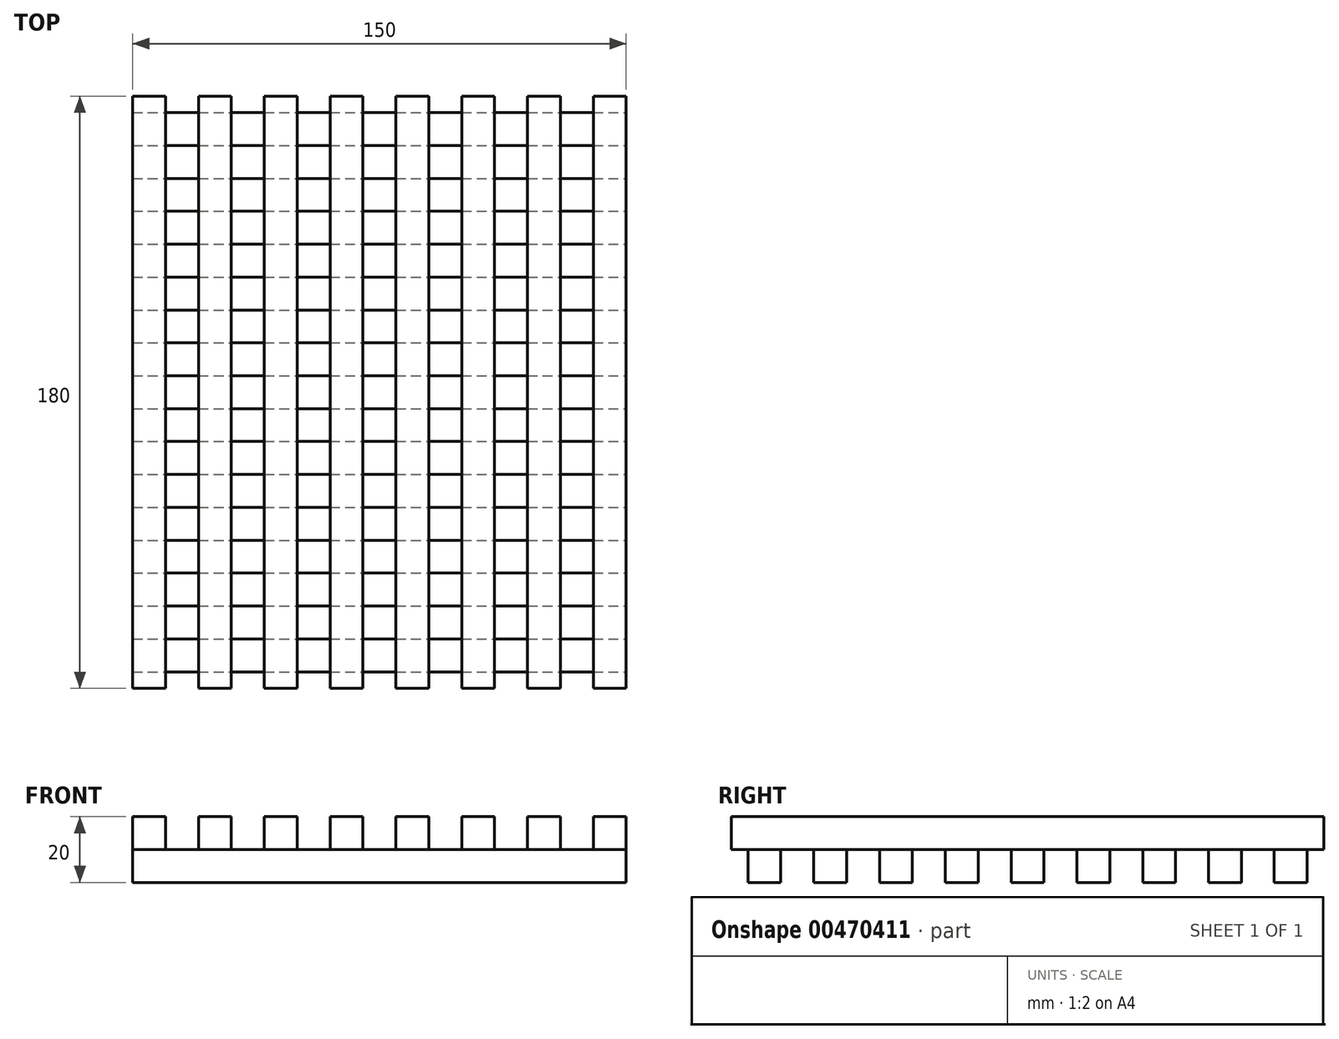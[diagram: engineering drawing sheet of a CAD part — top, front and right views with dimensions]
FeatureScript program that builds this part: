
annotation { "Feature Type Name" : "Feature", "Feature Type Description" : "" }
export const myFeature = defineFeature(function(context is Context, id is Id, definition is map)
    precondition{}
    {
        {
            var Q0;
            Q0=qCreatedBy(makeId("Top.planeOp"),FACE);
            var sketch = newSketch(context, id + "F0", { "sketchPlane" : qUnion([Q0])});
            skLineSegment(sketch, "E0.bottom", {"start": v(-75, -5) * mm, "end": v(75, -5) * mm});
            skLineSegment(sketch, "E0.top", {"start": v(-75, -15) * mm, "end": v(75, -15) * mm});
            skLineSegment(sketch, "E0.left", {"start": v(-75, -5) * mm, "end": v(-75, -15) * mm});
            skLineSegment(sketch, "E0.right", {"start": v(75, -5) * mm, "end": v(75, -15) * mm});
            skPoint(sketch, "E0.middle", {"position": v(0, -10) * mm});
            skLineSegment(sketch, "E1.bottom", {"start": v(-75, 15) * mm, "end": v(75, 15) * mm});
            skLineSegment(sketch, "E1.top", {"start": v(-75, 5) * mm, "end": v(75, 5) * mm});
            skLineSegment(sketch, "E1.left", {"start": v(-75, 15) * mm, "end": v(-75, 5) * mm});
            skLineSegment(sketch, "E1.right", {"start": v(75, 15) * mm, "end": v(75, 5) * mm});
            skPoint(sketch, "E1.middle", {"position": v(0, 10) * mm});
            skLineSegment(sketch, "E2.bottom", {"start": v(-75, -45) * mm, "end": v(75, -45) * mm});
            skLineSegment(sketch, "E2.top", {"start": v(-75, -55) * mm, "end": v(75, -55) * mm});
            skLineSegment(sketch, "E2.left", {"start": v(-75, -45) * mm, "end": v(-75, -55) * mm});
            skLineSegment(sketch, "E2.right", {"start": v(75, -45) * mm, "end": v(75, -55) * mm});
            skPoint(sketch, "E2.middle", {"position": v(0, -50) * mm});
            skLineSegment(sketch, "E3.bottom", {"start": v(-75, -25) * mm, "end": v(75, -25) * mm});
            skLineSegment(sketch, "E3.top", {"start": v(-75, -35) * mm, "end": v(75, -35) * mm});
            skLineSegment(sketch, "E3.left", {"start": v(-75, -25) * mm, "end": v(-75, -35) * mm});
            skLineSegment(sketch, "E3.right", {"start": v(75, -25) * mm, "end": v(75, -35) * mm});
            skPoint(sketch, "E3.middle", {"position": v(0, -30) * mm});
            skLineSegment(sketch, "E4.bottom", {"start": v(-75, -65) * mm, "end": v(75, -65) * mm});
            skLineSegment(sketch, "E4.top", {"start": v(-75, -75) * mm, "end": v(75, -75) * mm});
            skLineSegment(sketch, "E4.left", {"start": v(-75, -65) * mm, "end": v(-75, -75) * mm});
            skLineSegment(sketch, "E4.right", {"start": v(75, -65) * mm, "end": v(75, -75) * mm});
            skPoint(sketch, "E4.middle", {"position": v(0, -70) * mm});
            skLineSegment(sketch, "E5.bottom", {"start": v(-75, 35) * mm, "end": v(75, 35) * mm});
            skLineSegment(sketch, "E5.top", {"start": v(-75, 25) * mm, "end": v(75, 25) * mm});
            skLineSegment(sketch, "E5.left", {"start": v(-75, 35) * mm, "end": v(-75, 25) * mm});
            skLineSegment(sketch, "E5.right", {"start": v(75, 35) * mm, "end": v(75, 25) * mm});
            skPoint(sketch, "E5.middle", {"position": v(0, 30) * mm});
            skLineSegment(sketch, "E6.bottom", {"start": v(-75, 55) * mm, "end": v(75, 55) * mm});
            skLineSegment(sketch, "E6.top", {"start": v(-75, 45) * mm, "end": v(75, 45) * mm});
            skLineSegment(sketch, "E6.left", {"start": v(-75, 55) * mm, "end": v(-75, 45) * mm});
            skLineSegment(sketch, "E6.right", {"start": v(75, 55) * mm, "end": v(75, 45) * mm});
            skPoint(sketch, "E6.middle", {"position": v(0, 50) * mm});
            skLineSegment(sketch, "E7.bottom", {"start": v(-75, 75) * mm, "end": v(75, 75) * mm});
            skLineSegment(sketch, "E7.top", {"start": v(-75, 65) * mm, "end": v(75, 65) * mm});
            skLineSegment(sketch, "E7.left", {"start": v(-75, 75) * mm, "end": v(-75, 65) * mm});
            skLineSegment(sketch, "E7.right", {"start": v(75, 75) * mm, "end": v(75, 65) * mm});
            skPoint(sketch, "E7.middle", {"position": v(0, 70) * mm});
            skLineSegment(sketch, "E8.bottom", {"start": v(-75, 95) * mm, "end": v(75, 95) * mm});
            skLineSegment(sketch, "E8.top", {"start": v(-75, 85) * mm, "end": v(75, 85) * mm});
            skLineSegment(sketch, "E8.left", {"start": v(-75, 95) * mm, "end": v(-75, 85) * mm});
            skLineSegment(sketch, "E8.right", {"start": v(75, 95) * mm, "end": v(75, 85) * mm});
            skPoint(sketch, "E8.middle", {"position": v(0, 90) * mm});
            skSolve(sketch);
        }
        {
            var Q0;
            Q0=makeQuery(id+"F0.imprint","IMPRINT",FACE,{"disambiguationData":[TD([[makeQuery(id+"F0.imprint","IMPRINT",EDGE,{"derivedFrom":sQuery(id+"F0.wireOp",EDGE,"E6.bottom")}),-1.0]])]});
            var Q1;
            Q1=makeQuery(id+"F0.imprint","IMPRINT",FACE,{"disambiguationData":[TD([[makeQuery(id+"F0.imprint","IMPRINT",EDGE,{"derivedFrom":sQuery(id+"F0.wireOp",EDGE,"E5.bottom")}),-1.0]])]});
            var Q2;
            Q2=makeQuery(id+"F0.imprint","IMPRINT",FACE,{"disambiguationData":[TD([[makeQuery(id+"F0.imprint","IMPRINT",EDGE,{"derivedFrom":sQuery(id+"F0.wireOp",EDGE,"E1.bottom")}),-1.0]])]});
            var Q3;
            Q3=makeQuery(id+"F0.imprint","IMPRINT",FACE,{"disambiguationData":[TD([[makeQuery(id+"F0.imprint","IMPRINT",EDGE,{"derivedFrom":sQuery(id+"F0.wireOp",EDGE,"E0.bottom")}),-1.0]])]});
            var Q4;
            Q4=makeQuery(id+"F0.imprint","IMPRINT",FACE,{"disambiguationData":[TD([[makeQuery(id+"F0.imprint","IMPRINT",EDGE,{"derivedFrom":sQuery(id+"F0.wireOp",EDGE,"E3.bottom")}),-1.0]])]});
            var Q5;
            Q5=makeQuery(id+"F0.imprint","IMPRINT",FACE,{"disambiguationData":[TD([[makeQuery(id+"F0.imprint","IMPRINT",EDGE,{"derivedFrom":sQuery(id+"F0.wireOp",EDGE,"E2.bottom")}),-1.0]])]});
            var Q6;
            Q6=makeQuery(id+"F0.imprint","IMPRINT",FACE,{"disambiguationData":[TD([[makeQuery(id+"F0.imprint","IMPRINT",EDGE,{"derivedFrom":sQuery(id+"F0.wireOp",EDGE,"E4.bottom")}),-1.0]])]});
            var Q7;
            Q7=makeQuery(id+"F0.imprint","IMPRINT",FACE,{"disambiguationData":[TD([[makeQuery(id+"F0.imprint","IMPRINT",EDGE,{"derivedFrom":sQuery(id+"F0.wireOp",EDGE,"f626e70f-c8a2-40ae-a205-73b3921139d5.bottom")}),-1.0]])]});
            extrude(context, id + "F1", {"entities" : qUnion([Q0, Q1, Q2, Q3, Q4, Q5, Q6, Q7]), "depth" : 10 * mm});
        }
        {
            var Q0;
            Q0=makeQuery(id+"F0.imprint","IMPRINT",FACE,{"disambiguationData":[TD([[makeQuery(id+"F0.imprint","IMPRINT",EDGE,{"derivedFrom":sQuery(id+"F0.wireOp",EDGE,"E8.bottom")}),-1.0]])]});
            var Q1;
            Q1=makeQuery(id+"F0.imprint","IMPRINT",FACE,{"disambiguationData":[TD([[makeQuery(id+"F0.imprint","IMPRINT",EDGE,{"derivedFrom":sQuery(id+"F0.wireOp",EDGE,"E7.bottom")}),-1.0]])]});
            var Q2;
            Q2=makeQuery(id+"F0.imprint","IMPRINT",FACE,{"disambiguationData":[TD([[makeQuery(id+"F0.imprint","IMPRINT",EDGE,{"derivedFrom":sQuery(id+"F0.wireOp",EDGE,"E6.bottom")}),-1.0]])]});
            var Q3;
            Q3=makeQuery(id+"F0.imprint","IMPRINT",FACE,{"disambiguationData":[TD([[makeQuery(id+"F0.imprint","IMPRINT",EDGE,{"derivedFrom":sQuery(id+"F0.wireOp",EDGE,"E5.bottom")}),-1.0]])]});
            var Q4;
            Q4=makeQuery(id+"F0.imprint","IMPRINT",FACE,{"disambiguationData":[TD([[makeQuery(id+"F0.imprint","IMPRINT",EDGE,{"derivedFrom":sQuery(id+"F0.wireOp",EDGE,"E1.bottom")}),-1.0]])]});
            var Q5;
            Q5=makeQuery(id+"F0.imprint","IMPRINT",FACE,{"disambiguationData":[TD([[makeQuery(id+"F0.imprint","IMPRINT",EDGE,{"derivedFrom":sQuery(id+"F0.wireOp",EDGE,"E0.bottom")}),-1.0]])]});
            var Q6;
            Q6=makeQuery(id+"F0.imprint","IMPRINT",FACE,{"disambiguationData":[TD([[makeQuery(id+"F0.imprint","IMPRINT",EDGE,{"derivedFrom":sQuery(id+"F0.wireOp",EDGE,"E3.bottom")}),-1.0]])]});
            var Q7;
            Q7=makeQuery(id+"F0.imprint","IMPRINT",FACE,{"disambiguationData":[TD([[makeQuery(id+"F0.imprint","IMPRINT",EDGE,{"derivedFrom":sQuery(id+"F0.wireOp",EDGE,"E2.bottom")}),-1.0]])]});
            var Q8;
            Q8=makeQuery(id+"F0.imprint","IMPRINT",FACE,{"disambiguationData":[TD([[makeQuery(id+"F0.imprint","IMPRINT",EDGE,{"derivedFrom":sQuery(id+"F0.wireOp",EDGE,"E4.bottom")}),-1.0]])]});
            extrude(context, id + "F2", {"entities" : qUnion([Q0, Q1, Q2, Q3, Q4, Q5, Q6, Q7, Q8]), "depth" : 10 * mm});
        }
        {
            var Q0;
            Q0=makeQuery(id+"F1.opExtrude","CAP_FACE",FACE,{"disambiguationData":[OSD([sQuery(id+"F0.wireOp",EDGE,"E1.bottom"),sQuery(id+"F0.wireOp",EDGE,"E1.top"),sQuery(id+"F0.wireOp",EDGE,"E1.left"),sQuery(id+"F0.wireOp",EDGE,"E1.right")])],"isStart":false});
            var sketch = newSketch(context, id + "F3", { "sketchPlane" : qUnion([Q0])});
            skLineSegment(sketch, "E9.bottom", {"start": v(75, 100) * mm, "end": v(65, 100) * mm});
            skLineSegment(sketch, "E9.top", {"start": v(75, -80) * mm, "end": v(65, -80) * mm});
            skLineSegment(sketch, "E9.left", {"start": v(75, 100) * mm, "end": v(75, -80) * mm});
            skLineSegment(sketch, "E9.right", {"start": v(65, 100) * mm, "end": v(65, -80) * mm});
            skLineSegment(sketch, "E10.bottom", {"start": v(55, 100) * mm, "end": v(45, 100) * mm});
            skLineSegment(sketch, "E10.top", {"start": v(55, -80) * mm, "end": v(45, -80) * mm});
            skLineSegment(sketch, "E10.left", {"start": v(55, 100) * mm, "end": v(55, -80) * mm});
            skLineSegment(sketch, "E10.right", {"start": v(45, 100) * mm, "end": v(45, -80) * mm});
            skLineSegment(sketch, "E11.bottom", {"start": v(35, 100) * mm, "end": v(25, 100) * mm});
            skLineSegment(sketch, "E11.top", {"start": v(35, -80) * mm, "end": v(25, -80) * mm});
            skLineSegment(sketch, "E11.left", {"start": v(35, 100) * mm, "end": v(35, -80) * mm});
            skLineSegment(sketch, "E11.right", {"start": v(25, 100) * mm, "end": v(25, -80) * mm});
            skLineSegment(sketch, "E12.bottom", {"start": v(15, 100) * mm, "end": v(5, 100) * mm});
            skLineSegment(sketch, "E12.top", {"start": v(15, -80) * mm, "end": v(5, -80) * mm});
            skLineSegment(sketch, "E12.left", {"start": v(15, 100) * mm, "end": v(15, -80) * mm});
            skLineSegment(sketch, "E12.right", {"start": v(5, 100) * mm, "end": v(5, -80) * mm});
            skLineSegment(sketch, "E13.bottom", {"start": v(-5, 100) * mm, "end": v(-15, 100) * mm});
            skLineSegment(sketch, "E13.top", {"start": v(-5, -80) * mm, "end": v(-15, -80) * mm});
            skLineSegment(sketch, "E13.left", {"start": v(-5, 100) * mm, "end": v(-5, -80) * mm});
            skLineSegment(sketch, "E13.right", {"start": v(-15, 100) * mm, "end": v(-15, -80) * mm});
            skLineSegment(sketch, "E14.bottom", {"start": v(-25, 100) * mm, "end": v(-35, 100) * mm});
            skLineSegment(sketch, "E14.top", {"start": v(-25, -80) * mm, "end": v(-35, -80) * mm});
            skLineSegment(sketch, "E14.left", {"start": v(-25, 100) * mm, "end": v(-25, -80) * mm});
            skLineSegment(sketch, "E14.right", {"start": v(-35, 100) * mm, "end": v(-35, -80) * mm});
            skLineSegment(sketch, "E15.bottom", {"start": v(-45, 100) * mm, "end": v(-55, 100) * mm});
            skLineSegment(sketch, "E15.top", {"start": v(-45, -80) * mm, "end": v(-55, -80) * mm});
            skLineSegment(sketch, "E15.left", {"start": v(-45, 100) * mm, "end": v(-45, -80) * mm});
            skLineSegment(sketch, "E15.right", {"start": v(-55, 100) * mm, "end": v(-55, -80) * mm});
            skLineSegment(sketch, "E16.bottom", {"start": v(-65, 100) * mm, "end": v(-75, 100) * mm});
            skLineSegment(sketch, "E16.top", {"start": v(-65, -80) * mm, "end": v(-75, -80) * mm});
            skLineSegment(sketch, "E16.left", {"start": v(-65, 100) * mm, "end": v(-65, -80) * mm});
            skLineSegment(sketch, "E16.right", {"start": v(-75, 100) * mm, "end": v(-75, -80) * mm});
            skSolve(sketch);
        }
        {
            var Q0;
            Q0 = qSketchRegion(id + "F3", true);
            extrude(context, id + "F4", {"entities" : qUnion([Q0]), "depth" : 10 * mm});
        }
    });
